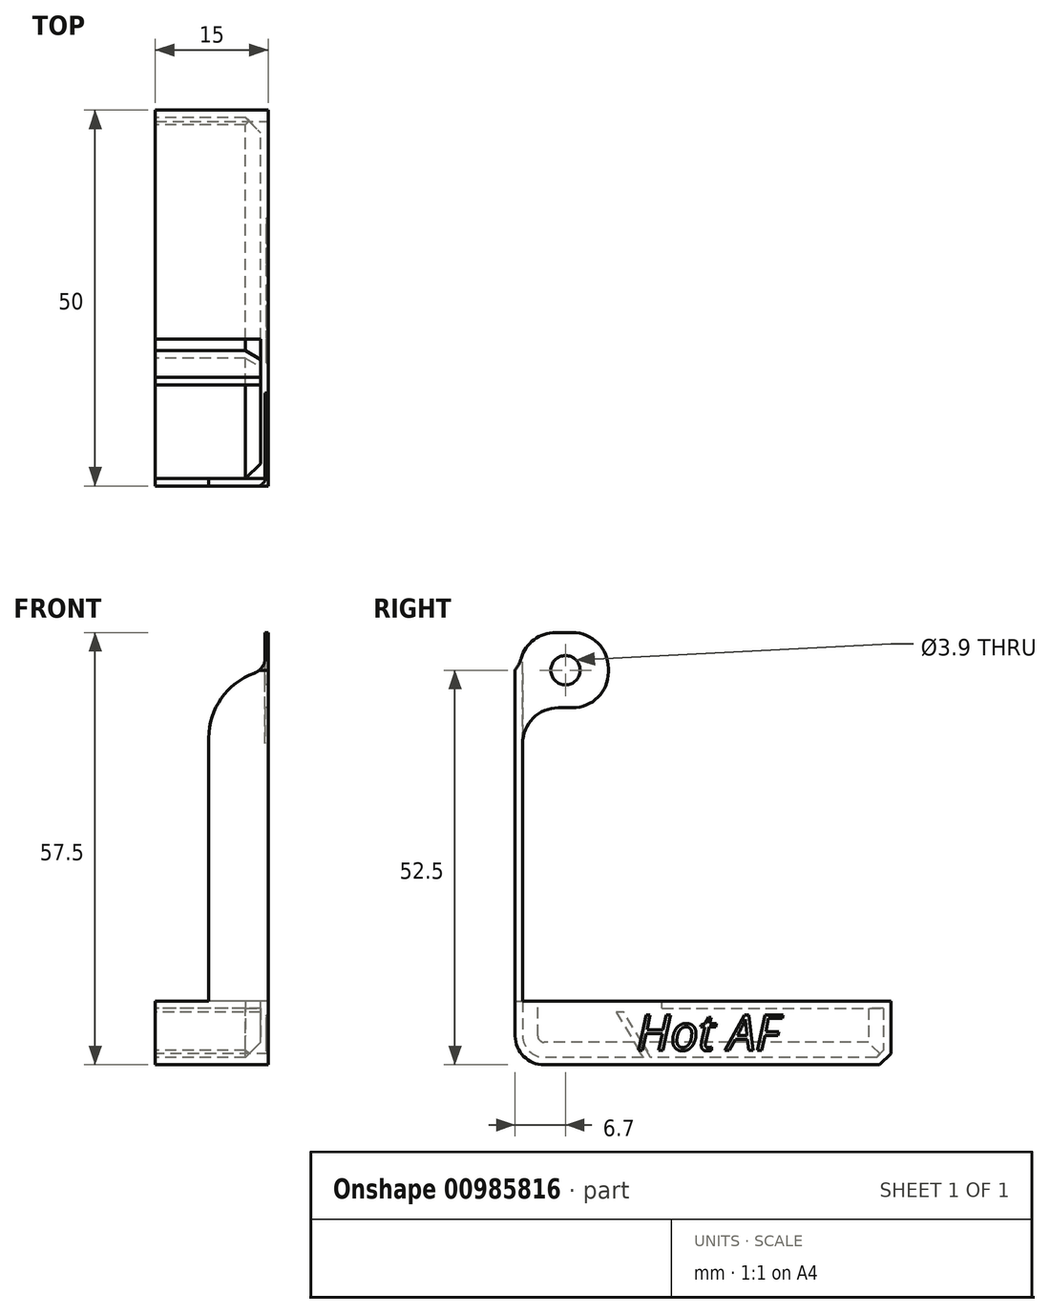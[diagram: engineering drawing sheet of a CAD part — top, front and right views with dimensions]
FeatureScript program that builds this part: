
annotation { "Feature Type Name" : "Feature", "Feature Type Description" : "" }
export const myFeature = defineFeature(function(context is Context, id is Id, definition is map)
    precondition{}
    {
        {
            var Q0;
            Q0=qCreatedBy(makeId("Right.planeOp"),FACE);
            var sketch = newSketch(context, id + "F0", { "sketchPlane" : qUnion([Q0])});
            skCircle(sketch, "E0", {"center": v(0, 0) * mm, "radius": 1.95 * mm});
            skLineSegment(sketch, "E1.bottom", {"start": v(5.7, 5) * mm, "end": v(-5.7, 5) * mm});
            skLineSegment(sketch, "E1.top", {"start": v(5.7, -5) * mm, "end": v(-5.7, -5) * mm});
            skLineSegment(sketch, "E1.left", {"start": v(5.7, 5) * mm, "end": v(5.7, -5) * mm});
            skLineSegment(sketch, "E1.right", {"start": v(-5.7, 5) * mm, "end": v(-5.7, -5) * mm});
            skLineSegment(sketch, "E2", {"start": v(-5.7, 0) * mm, "end": v(-6.7, 0) * mm});
            skLineSegment(sketch, "E3", {"start": v(-6.7, 0) * mm, "end": v(-6.7, -44) * mm});
            skLineSegment(sketch, "E4", {"start": v(-6.7, -44) * mm, "end": v(-5.7, -44) * mm});
            skLineSegment(sketch, "E5", {"start": v(-5.7, -44) * mm, "end": v(-5.7, -5) * mm});
            skLineSegment(sketch, "E6.bottom", {"start": v(-6.7, -44) * mm, "end": v(12.85, -44) * mm});
            skLineSegment(sketch, "E6.top", {"start": v(-6.7, -52.5) * mm, "end": v(12.85, -52.5) * mm});
            skLineSegment(sketch, "E6.left", {"start": v(-6.7, -44) * mm, "end": v(-6.7, -52.5) * mm});
            skLineSegment(sketch, "E6.right", {"start": v(12.85, -44) * mm, "end": v(12.85, -52.5) * mm});
            skLineSegment(sketch, "E7.bottom", {"start": v(12.85, -44) * mm, "end": v(43.3, -44) * mm});
            skLineSegment(sketch, "E7.top", {"start": v(12.85, -52.5) * mm, "end": v(43.3, -52.5) * mm});
            skLineSegment(sketch, "E7.right", {"start": v(43.3, -44) * mm, "end": v(43.3, -52.5) * mm});
            skSolve(sketch);
        }
        {
            var Q0;
            Q0=makeQuery(id+"F0.imprint","IMPRINT",FACE,{"disambiguationData":[TD([[makeQuery(id+"F0.imprint","IMPRINT",EDGE,{"derivedFrom":sQuery(id+"F0.wireOp",EDGE,"E0")}),-1.0]])]});
            var Q1;
            {var subQ0=sQuery(id+"F0.wireOp",EDGE,"E2");Q1=makeQuery(id+"F0.imprint","IMPRINT",FACE,{"disambiguationData":[TD([[makeQuery(id+"F0.imprint","IMPRINT",EDGE,{"derivedFrom":subQ0}),1.0]])]});}
            var Q2;
            Q2=makeQuery(id+"F0.imprint","IMPRINT",FACE,{"disambiguationData":[TD([[makeQuery(id+"F0.imprint","IMPRINT",EDGE,{"derivedFrom":sQuery(id+"F0.wireOp",EDGE,"E4")}),-1.0]])]});
            var Q3;
            Q3=makeQuery(id+"F0.imprint","IMPRINT",FACE,{"disambiguationData":[TD([[makeQuery(id+"F0.imprint","IMPRINT",EDGE,{"derivedFrom":sQuery(id+"F0.wireOp",EDGE,"E6.right")}),1.0]])]});
            extrude(context, id + "F1", {"entities" : qUnion([Q0, Q1, Q2, Q3]), "depth" : .4 * mm, "offsetDistance" : 25 * mm});
        }
        {
            var Q0;
            Q0=makeQuery(id+"F0.imprint","IMPRINT",FACE,{"disambiguationData":[TD([[makeQuery(id+"F0.imprint","IMPRINT",EDGE,{"derivedFrom":sQuery(id+"F0.wireOp",EDGE,"E4")}),-1.0]])]});
            var Q1;
            Q1=makeQuery(id+"F0.imprint","IMPRINT",FACE,{"disambiguationData":[TD([[makeQuery(id+"F0.imprint","IMPRINT",EDGE,{"derivedFrom":sQuery(id+"F0.wireOp",EDGE,"E6.right")}),1.0]])]});
            extrude(context, id + "F2", {"entities" : qUnion([Q0, Q1]), "operationType" : NewBodyOperationType.ADD, "oppositeDirection" : true, "depth" : 14.6 * mm, "offsetDistance" : 25 * mm});
        }
        {
            var Q0;
            Q0=makeQuery(id+"F1.opExtrude","SWEPT_EDGE",EDGE,{"disambiguationData":[OSD([sQuery(id+"F0.wireOp",EDGE,"E1.right"),sQuery(id+"F0.wireOp",EDGE,"E2")])]});
            fillet(context, id + "F3", {"entities" : qUnion([Q0]), "radius" : 5 * mm, "tangentPropagation" : true, "allowEdgeOverflow" : false});
        }
        {
            var Q0;
            Q0=makeQuery(id+"F1.opExtrude","SWEPT_EDGE",EDGE,{"disambiguationData":[OSD([sQuery(id+"F0.wireOp",EDGE,"E1.bottom"),sQuery(id+"F0.wireOp",EDGE,"E1.right")])]});
            var Q1;
            Q1=makeQuery(id+"F1.opExtrude","SWEPT_EDGE",EDGE,{"disambiguationData":[OSD([sQuery(id+"F0.wireOp",EDGE,"E1.bottom"),sQuery(id+"F0.wireOp",EDGE,"E1.left")])]});
            var Q2;
            Q2=makeQuery(id+"F1.opExtrude","SWEPT_EDGE",EDGE,{"disambiguationData":[OSD([sQuery(id+"F0.wireOp",EDGE,"E1.top"),sQuery(id+"F0.wireOp",EDGE,"E1.left")])]});
            var Q3;
            Q3=makeQuery(id+"F1.opExtrude","SWEPT_EDGE",EDGE,{"disambiguationData":[OSD([sQuery(id+"F0.wireOp",EDGE,"E1.top"),sQuery(id+"F0.wireOp",EDGE,"E1.right"),sQuery(id+"F0.wireOp",EDGE,"E5")])]});
            fillet(context, id + "F4", {"entities" : qUnion([Q0, Q1, Q2, Q3]), "radius" : 4.76 * mm, "tangentPropagation" : true, "allowEdgeOverflow" : false});
        }
        {
            var Q0;
            {var subQ0=sQuery(id+"F0.wireOp",EDGE,"E6.left");var subQ1=sQuery(id+"F0.wireOp",EDGE,"E6.top");Q0=makeQuery(id+"F2.boolean.opBoolean","MERGE",EDGE,{"derivedFrom":[makeQuery(id+"F1.opExtrude","SWEPT_EDGE",EDGE,{"disambiguationData":[OSD([subQ1,subQ0])]}),makeQuery(id+"F2.opExtrude","SWEPT_EDGE",EDGE,{"disambiguationData":[OSD([subQ1,subQ0])]})]});}
            fillet(context, id + "F5", {"entities" : qUnion([Q0]), "radius" : 3.86 * mm, "tangentPropagation" : true, "allowEdgeOverflow" : false});
        }
        {
            var Q0;
            {var subQ0=sQuery(id+"F0.wireOp",EDGE,"E7.right");var subQ1=sQuery(id+"F0.wireOp",EDGE,"E7.top");Q0=makeQuery(id+"F2.boolean.opBoolean","MERGE",EDGE,{"derivedFrom":[makeQuery(id+"F1.opExtrude","SWEPT_EDGE",EDGE,{"disambiguationData":[OSD([subQ1,subQ0])]}),makeQuery(id+"F2.opExtrude","SWEPT_EDGE",EDGE,{"disambiguationData":[OSD([subQ1,subQ0])]})]});}
            chamfer(context, id + "F6", {"entities" : qUnion([Q0]), "width" : 1.5 * mm, "tangentPropagation" : true});
        }
        {
            var Q0;
            {var subQ0=sQuery(id+"F0.wireOp",EDGE,"E2");Q0=makeQuery(id+"F0.imprint","IMPRINT",FACE,{"disambiguationData":[TD([[makeQuery(id+"F0.imprint","IMPRINT",EDGE,{"derivedFrom":subQ0}),1.0]])]});}
            extrude(context, id + "F7", {"entities" : qUnion([Q0]), "operationType" : NewBodyOperationType.ADD, "oppositeDirection" : true, "depth" : 7.5 * mm, "offsetDistance" : 25 * mm});
        }
        {
            var Q0;
            Q0=makeQuery(id+"F7.opExtrude","CAP_EDGE",EDGE,{"disambiguationData":[OSD([sQuery(id+"F0.wireOp",EDGE,"E2")])],"isStart":false});
            var Q1;
            Q1=makeQuery(id+"F7.opExtrude","CAP_EDGE",EDGE,{"disambiguationData":[OSD([sQuery(id+"F0.wireOp",EDGE,"E4")])],"isStart":false});
            fillet(context, id + "F8", {"entities" : qUnion([Q0, Q1]), "radius" : 9.17 * mm, "tangentPropagation" : true, "allowEdgeOverflow" : false});
        }
        {
            var Q0;
            {var subQ0=sQuery(id+"F0.wireOp",EDGE,"E2");Q0=makeQuery(id+"F8.opFillet","BLEND_EDGE",EDGE,{"blendedFrom":[makeQuery(id+"F7.opExtrude","CAP_EDGE",EDGE,{"disambiguationData":[OSD([subQ0])],"isStart":false}),makeQuery(id+"F1.opExtrude","CAP_FACE",FACE,{"disambiguationData":[OSD([sQuery(id+"F0.wireOp",EDGE,"E0"),sQuery(id+"F0.wireOp",EDGE,"E1.bottom"),sQuery(id+"F0.wireOp",EDGE,"E1.top"),sQuery(id+"F0.wireOp",EDGE,"E1.left"),sQuery(id+"F0.wireOp",EDGE,"E1.right"),subQ0,sQuery(id+"F0.wireOp",EDGE,"E3"),sQuery(id+"F0.wireOp",EDGE,"E5"),sQuery(id+"F0.wireOp",EDGE,"E6.bottom"),sQuery(id+"F0.wireOp",EDGE,"E6.top"),sQuery(id+"F0.wireOp",EDGE,"E6.left"),sQuery(id+"F0.wireOp",EDGE,"E7.bottom"),sQuery(id+"F0.wireOp",EDGE,"E7.top"),sQuery(id+"F0.wireOp",EDGE,"E7.right")])],"isStart":true})],"blendedInto":[makeQuery(id+"F1.opExtrude","CAP_FACE",FACE,{"disambiguationData":[OSD([sQuery(id+"F0.wireOp",EDGE,"E0"),sQuery(id+"F0.wireOp",EDGE,"E1.bottom"),sQuery(id+"F0.wireOp",EDGE,"E1.top"),sQuery(id+"F0.wireOp",EDGE,"E1.left"),sQuery(id+"F0.wireOp",EDGE,"E1.right"),subQ0,sQuery(id+"F0.wireOp",EDGE,"E3"),sQuery(id+"F0.wireOp",EDGE,"E5"),sQuery(id+"F0.wireOp",EDGE,"E6.bottom"),sQuery(id+"F0.wireOp",EDGE,"E6.top"),sQuery(id+"F0.wireOp",EDGE,"E6.left"),sQuery(id+"F0.wireOp",EDGE,"E7.bottom"),sQuery(id+"F0.wireOp",EDGE,"E7.top"),sQuery(id+"F0.wireOp",EDGE,"E7.right")])],"isStart":true})]});}
            fillet(context, id + "F9", {"entities" : qUnion([Q0]), "radius" : 2.16 * mm, "tangentPropagation" : true, "allowEdgeOverflow" : false});
        }
        {
            var Q0;
            Q0=makeQuery(id+"F1.opExtrude","CAP_FACE",FACE,{"disambiguationData":[OSD([sQuery(id+"F0.wireOp",EDGE,"E0"),sQuery(id+"F0.wireOp",EDGE,"E1.bottom"),sQuery(id+"F0.wireOp",EDGE,"E1.top"),sQuery(id+"F0.wireOp",EDGE,"E1.left"),sQuery(id+"F0.wireOp",EDGE,"E1.right"),sQuery(id+"F0.wireOp",EDGE,"E2"),sQuery(id+"F0.wireOp",EDGE,"E3"),sQuery(id+"F0.wireOp",EDGE,"E5"),sQuery(id+"F0.wireOp",EDGE,"E6.bottom"),sQuery(id+"F0.wireOp",EDGE,"E6.top"),sQuery(id+"F0.wireOp",EDGE,"E6.left"),sQuery(id+"F0.wireOp",EDGE,"E7.bottom"),sQuery(id+"F0.wireOp",EDGE,"E7.top"),sQuery(id+"F0.wireOp",EDGE,"E7.right")])],"isStart":false});
            var sketch = newSketch(context, id + "F10", { "sketchPlane" : qUnion([Q0])});
            skText(sketch, "E8", { "text": "Hot AF", "fontName": "OpenSans-Italic.ttf"});
            const initialGuessF10  = {"E8": [0.00942, -0.0506, 1, 0, 0.0048]};
            skSetInitialGuess(sketch, initialGuessF10);
            skSolve(sketch);
        }
        {
            var Q0;
            Q0=makeQuery(id+"F2.opExtrude","CAP_FACE",FACE,{"disambiguationData":[OSD([sQuery(id+"F0.wireOp",EDGE,"E4"),sQuery(id+"F0.wireOp",EDGE,"E6.bottom"),sQuery(id+"F0.wireOp",EDGE,"E6.top"),sQuery(id+"F0.wireOp",EDGE,"E6.left"),sQuery(id+"F0.wireOp",EDGE,"E7.bottom"),sQuery(id+"F0.wireOp",EDGE,"E7.top"),sQuery(id+"F0.wireOp",EDGE,"E7.right")])],"isStart":false});
            var sketch = newSketch(context, id + "F11", { "sketchPlane" : qUnion([Q0])});
            skLineSegment(sketch, "E9", {"start": v(-12.83, -45) * mm, "end": v(-12.83, -44) * mm});
            skLineSegment(sketch, "E10", {"start": v(5.7, -45) * mm, "end": v(5.7, -44) * mm});
            skLineSegment(sketch, "E11.0", {"start": v(-12.83, -45) * mm, "end": v(-42.3, -45) * mm});
            skLineSegment(sketch, "E11.1", {"start": v(5.7, -45) * mm, "end": v(5.7, -45) * mm});
            skLineSegment(sketch, "E11.2", {"start": v(-42.3, -50.59) * mm, "end": v(-41.39, -51.5) * mm});
            skLineSegment(sketch, "E11.3", {"start": v(-41.39, -51.5) * mm, "end": v(-11.33, -51.5) * mm});
            skArc(sketch, "E11.4", {"start": v(2.84, -51.5) * mm, "mid": v(4.86, -50.66) * mm, "end": v(5.7, -48.64) * mm});
            skLineSegment(sketch, "E11.5", {"start": v(-42.3, -45) * mm, "end": v(-42.3, -50.59) * mm});
            skLineSegment(sketch, "E11.6", {"start": v(5.7, -48.64) * mm, "end": v(5.7, -45) * mm});
            skLineSegment(sketch, "E12", {"start": v(-11.33, -51.5) * mm, "end": v(-7.75, -45.48) * mm});
            skLineSegment(sketch, "E13", {"start": v(-7.75, -45.48) * mm, "end": v(-6.75, -45.48) * mm});
            skLineSegment(sketch, "E14", {"start": v(-6.75, -45.48) * mm, "end": v(-10.33, -51.5) * mm});
            skLineSegment(sketch, "E15.trimOffspring", {"start": v(-10.33, -51.5) * mm, "end": v(2.84, -51.5) * mm});
            skSolve(sketch);
        }
        {
            var Q0;
            {var subQ0=sQuery(id+"F11.wireOp",EDGE,"E9");Q0=makeQuery(id+"F11.imprint","IMPRINT",FACE,{"disambiguationData":[TD([[makeQuery(id+"F11.imprint","IMPRINT",EDGE,{"derivedFrom":subQ0}),-1.0]])]});}
            extrude(context, id + "F12", {"entities" : qUnion([Q0]), "operationType" : NewBodyOperationType.REMOVE, "oppositeDirection" : true, "depth" : 14 * mm, "offsetDistance" : 25 * mm});
        }
        {
            var Q0;
            Q0=makeQuery(id+"F12.boolean.opBoolean","COPY",EDGE,{"derivedFrom":makeQuery(id+"F12.opExtrude","CAP_EDGE",EDGE,{"disambiguationData":[OSD([sQuery(id+"F11.wireOp",EDGE,"E11.3")])],"isStart":false})});
            var Q1;
            Q1=makeQuery(id+"F12.boolean.opBoolean","COPY",EDGE,{"derivedFrom":makeQuery(id+"F12.opExtrude","CAP_EDGE",EDGE,{"disambiguationData":[OSD([sQuery(id+"F11.wireOp",EDGE,"E11.2")])],"isStart":false})});
            var Q2;
            Q2=makeQuery(id+"F12.boolean.opBoolean","COPY",EDGE,{"derivedFrom":makeQuery(id+"F12.opExtrude","CAP_EDGE",EDGE,{"disambiguationData":[OSD([sQuery(id+"F11.wireOp",EDGE,"E11.5")])],"isStart":false})});
            var Q3;
            Q3=makeQuery(id+"F12.boolean.opBoolean","COPY",EDGE,{"derivedFrom":makeQuery(id+"F12.opExtrude","CAP_EDGE",EDGE,{"disambiguationData":[OSD([sQuery(id+"F11.wireOp",EDGE,"E15.trimOffspring")])],"isStart":false})});
            var Q4;
            Q4=makeQuery(id+"F12.boolean.opBoolean","COPY",EDGE,{"derivedFrom":makeQuery(id+"F12.opExtrude","CAP_EDGE",EDGE,{"disambiguationData":[OSD([sQuery(id+"F11.wireOp",EDGE,"E11.4")])],"isStart":false})});
            var Q5;
            Q5=makeQuery(id+"F12.boolean.opBoolean","COPY",EDGE,{"derivedFrom":makeQuery(id+"F12.opExtrude","CAP_EDGE",EDGE,{"disambiguationData":[OSD([sQuery(id+"F11.wireOp",EDGE,"E10"),sQuery(id+"F11.wireOp",EDGE,"E11.6")])],"isStart":false})});
            chamfer(context, id + "F13", {"entities" : qUnion([Q0, Q1, Q2, Q3, Q4, Q5]), "width" : 2 * mm, "tangentPropagation" : true});
        }
        {
            var Q0;
            Q0 = qSketchRegion(id + "F10", true);
            extrude(context, id + "F14", {"entities" : qUnion([Q0]), "operationType" : NewBodyOperationType.REMOVE, "oppositeDirection" : true, "depth" : .2 * mm, "offsetDistance" : 25 * mm});
        }
    });
